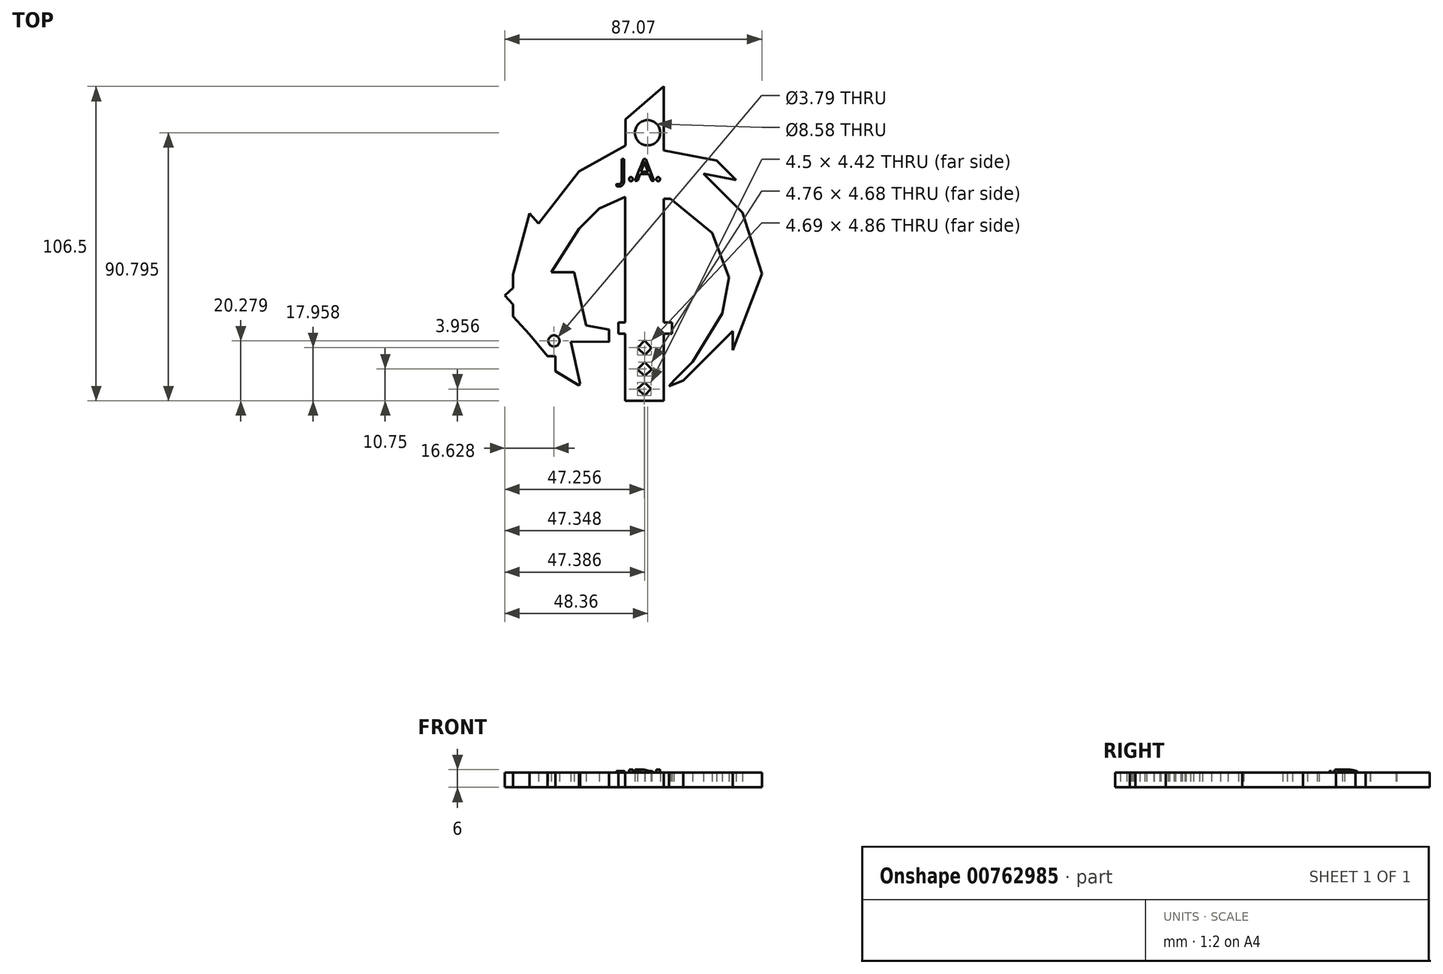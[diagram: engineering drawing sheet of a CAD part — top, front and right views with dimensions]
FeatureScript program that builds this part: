
annotation { "Feature Type Name" : "Feature", "Feature Type Description" : "" }
export const myFeature = defineFeature(function(context is Context, id is Id, definition is map)
    precondition{}
    {
        {
            var Q0;
            Q0=qCreatedBy(makeId("Top.planeOp"),FACE);
            var sketch = newSketch(context, id + "F0", { "sketchPlane" : qUnion([Q0])});
            skLineSegment(sketch, "E0", {"start": v(-26.03, -12.55) * mm, "end": v(-22.86, -26.95) * mm});
            skLineSegment(sketch, "E1", {"start": v(-22.86, -26.95) * mm, "end": v(-23.17, -27.48) * mm});
            skLineSegment(sketch, "E2", {"start": v(-23.17, -27.48) * mm, "end": v(-31.28, -22.62) * mm});
            skLineSegment(sketch, "E3", {"start": v(-31.28, -17.57) * mm, "end": v(-33.96, -17.57) * mm});
            skLineSegment(sketch, "E4", {"start": v(-33.96, -17.57) * mm, "end": v(-40.04, -10.17) * mm});
            skLineSegment(sketch, "E5", {"start": v(-40.04, -10.17) * mm, "end": v(-45.59, -4.1) * mm});
            skLineSegment(sketch, "E6", {"start": v(-45.59, -4.1) * mm, "end": v(-45.59, 0) * mm});
            skLineSegment(sketch, "E7", {"start": v(-45.59, 0) * mm, "end": v(-40.04, -6.08) * mm});
            skLineSegment(sketch, "E8", {"start": v(-40.04, -6.08) * mm, "end": v(-45.59, 0) * mm});
            skLineSegment(sketch, "E9", {"start": v(-45.59, 0) * mm, "end": v(-48.36, 3.04) * mm});
            skLineSegment(sketch, "E10", {"start": v(-48.36, 3.04) * mm, "end": v(-45.59, 5.57) * mm});
            skLineSegment(sketch, "E11", {"start": v(-45.59, 5.57) * mm, "end": v(-45.59, 10.17) * mm});
            skLineSegment(sketch, "E12", {"start": v(-45.59, 10.17) * mm, "end": v(-40.04, 30.79) * mm});
            skLineSegment(sketch, "E13", {"start": v(-40.04, 30.79) * mm, "end": v(-37, 27.45) * mm});
            skLineSegment(sketch, "E14", {"start": v(-37, 27.45) * mm, "end": v(-23.17, 45.06) * mm});
            skLineSegment(sketch, "E15", {"start": v(-23.17, 45.06) * mm, "end": v(-7.53, 53.78) * mm});
            skLineSegment(sketch, "E16", {"start": v(5.42, -9.9) * mm, "end": v(8.32, -9.9) * mm});
            skLineSegment(sketch, "E17", {"start": v(8.32, -9.9) * mm, "end": v(8.32, -6.08) * mm});
            skLineSegment(sketch, "E18", {"start": v(-7.53, 62.76) * mm, "end": v(5.42, 73.86) * mm});
            skLineSegment(sketch, "E19", {"start": v(5.42, 73.86) * mm, "end": v(5.42, -3.04) * mm});
            skLineSegment(sketch, "E20", {"start": v(5.42, -3.04) * mm, "end": v(0, 0) * mm});
            skLineSegment(sketch, "E21", {"start": v(5.42, -9.9) * mm, "end": v(5.42, -32.64) * mm});
            skLineSegment(sketch, "E22", {"start": v(-9.9, -6.08) * mm, "end": v(8.32, -6.08) * mm});
            skLineSegment(sketch, "E23", {"start": v(7.8, 35.8) * mm, "end": v(21.8, 24.18) * mm});
            skLineSegment(sketch, "E24", {"start": v(21.8, 24.18) * mm, "end": v(27.62, 9.12) * mm});
            skLineSegment(sketch, "E25", {"start": v(27.62, 9.12) * mm, "end": v(25.24, -3.04) * mm});
            skLineSegment(sketch, "E26", {"start": v(25.24, -3.04) * mm, "end": v(15.2, -19.42) * mm});
            skLineSegment(sketch, "E27", {"start": v(15.2, -19.42) * mm, "end": v(8.85, -25.77) * mm});
            skLineSegment(sketch, "E28", {"start": v(12.02, -25.77) * mm, "end": v(28.8, -8.98) * mm});
            skPoint(sketch, "E28.startSnap0", {"position": v(12.02, -22.6) * mm});
            skLineSegment(sketch, "E29", {"start": v(28.8, -8.98) * mm, "end": v(28.8, -15.46) * mm});
            skLineSegment(sketch, "E30", {"start": v(28.8, -15.46) * mm, "end": v(38.71, 10.44) * mm});
            skLineSegment(sketch, "E31", {"start": v(38.71, 10.44) * mm, "end": v(32.1, 31.05) * mm});
            skLineSegment(sketch, "E32", {"start": v(32.1, 31.05) * mm, "end": v(18.9, 44.26) * mm});
            skLineSegment(sketch, "E33", {"start": v(18.9, 44.26) * mm, "end": v(30, 42.15) * mm});
            skLineSegment(sketch, "E34", {"start": v(30, 42.15) * mm, "end": v(23.39, 48.76) * mm});
            skLineSegment(sketch, "E35", {"start": v(23.39, 48.76) * mm, "end": v(8.85, 51.52) * mm});
            skLineSegment(sketch, "E36", {"start": v(8.85, 51.52) * mm, "end": v(5.42, 52.18) * mm});
            skLineSegment(sketch, "E37", {"start": v(8.85, -25.77) * mm, "end": v(7.2, -27.75) * mm});
            skLineSegment(sketch, "E38", {"start": v(7.2, -27.75) * mm, "end": v(12.02, -25.77) * mm});
            skLineSegment(sketch, "E39", {"start": v(-26.03, -12.55) * mm, "end": v(-22.86, -12.59) * mm});
            skLineSegment(sketch, "E40", {"start": v(-22.86, -12.59) * mm, "end": v(-13.06, -12.7) * mm});
            skLineSegment(sketch, "E41", {"start": v(-13.06, -12.7) * mm, "end": v(-13.06, -8.59) * mm});
            skLineSegment(sketch, "E42", {"start": v(-13.06, -8.59) * mm, "end": v(-16.32, -7.97) * mm});
            skLineSegment(sketch, "E43", {"start": v(-16.32, -7.97) * mm, "end": v(-20.86, -7.1) * mm});
            skLineSegment(sketch, "E44", {"start": v(-20.86, -7.1) * mm, "end": v(-23.17, 3.39) * mm});
            skLineSegment(sketch, "E45", {"start": v(-23.17, 3.39) * mm, "end": v(-24.83, 10.91) * mm});
            skLineSegment(sketch, "E46", {"start": v(-24.83, 10.91) * mm, "end": v(-32.64, 10.91) * mm});
            skLineSegment(sketch, "E47", {"start": v(-32.64, 10.91) * mm, "end": v(-23.17, 25.64) * mm});
            skLineSegment(sketch, "E48", {"start": v(-23.17, 25.64) * mm, "end": v(-16.32, 32.49) * mm});
            skLineSegment(sketch, "E49", {"start": v(-16.32, 32.49) * mm, "end": v(-7.53, 36.43) * mm});
            skLineSegment(sketch, "E50", {"start": v(-31.28, -17.57) * mm, "end": v(-31.28, -22.62) * mm});
            skLineSegment(sketch, "E51", {"start": v(7.8, 35.8) * mm, "end": v(5.42, 35.83) * mm});
            skPoint(sketch, "E51.endSnap0", {"position": v(5.42, 35.41) * mm});
            skLineSegment(sketch, "E52", {"start": v(-7.6, -6.08) * mm, "end": v(5.42, -6.08) * mm});
            skLineSegment(sketch, "E53", {"start": v(5.42, -6.08) * mm, "end": v(5.42, -3.04) * mm});
            skLineSegment(sketch, "E54", {"start": v(0, 0) * mm, "end": v(-7.6, -3.04) * mm});
            skLineSegment(sketch, "E55", {"start": v(-7.6, -3.04) * mm, "end": v(-7.53, 62.76) * mm});
            skLineSegment(sketch, "E56", {"start": v(-7.6, -3.04) * mm, "end": v(-7.6, -6.08) * mm});
            skLineSegment(sketch, "E57", {"start": v(-9.9, -6.08) * mm, "end": v(-9.9, -9.9) * mm});
            skLineSegment(sketch, "E58", {"start": v(-9.9, -9.9) * mm, "end": v(-7.55, -9.9) * mm});
            skLineSegment(sketch, "E59", {"start": v(-7.55, -9.9) * mm, "end": v(-7.55, -32.64) * mm});
            skLineSegment(sketch, "E60", {"start": v(5.42, -32.64) * mm, "end": v(-7.55, -32.64) * mm});
            skCircle(sketch, "E61", {"center": v(-31.73, -12.36) * mm, "radius": 1.9 * mm});
            skLineSegment(sketch, "E62", {"start": v(-1.02, -12.25) * mm, "end": v(-3.35, -14.78) * mm});
            skLineSegment(sketch, "E63", {"start": v(-3.35, -14.78) * mm, "end": v(-0.83, -17.11) * mm});
            skLineSegment(sketch, "E64", {"start": v(-0.83, -17.11) * mm, "end": v(1.33, -14.78) * mm});
            skLineSegment(sketch, "E65", {"start": v(1.33, -14.78) * mm, "end": v(-1.02, -12.25) * mm});
            skLineSegment(sketch, "E66", {"start": v(-1.02, -19.55) * mm, "end": v(-3.35, -21.98) * mm});
            skLineSegment(sketch, "E67", {"start": v(-3.35, -21.98) * mm, "end": v(-1.02, -24.23) * mm});
            skLineSegment(sketch, "E68", {"start": v(-1.02, -24.23) * mm, "end": v(1.4, -21.98) * mm});
            skLineSegment(sketch, "E69", {"start": v(1.4, -21.98) * mm, "end": v(-1.02, -19.55) * mm});
            skLineSegment(sketch, "E70", {"start": v(-1.02, -26.47) * mm, "end": v(-3.35, -28.65) * mm});
            skLineSegment(sketch, "E71", {"start": v(-3.35, -28.65) * mm, "end": v(-1.02, -30.9) * mm});
            skLineSegment(sketch, "E72", {"start": v(-1.02, -30.9) * mm, "end": v(1.15, -28.65) * mm});
            skLineSegment(sketch, "E73", {"start": v(1.15, -28.65) * mm, "end": v(-1.02, -26.47) * mm});
            skCircle(sketch, "E74", {"center": v(0, 58.16) * mm, "radius": 4.29 * mm});
            skSolve(sketch);
        }
        {
            var Q0;
            {var subQ6=sQuery(id+"F0.wireOp",EDGE,"E18");var subQ8=sQuery(id+"F0.wireOp",EDGE,"E20");var subQ9=makeQuery(id+"F0.imprint","IMPRINT",EDGE,{"derivedFrom":subQ8});Q0=qUnion([makeQuery(id+"F0.imprint","IMPRINT",FACE,{"disambiguationData":[TD([[makeQuery(id+"F0.imprint","IMPRINT",EDGE,{"derivedFrom":sQuery(id+"F0.wireOp",EDGE,"E23")}),1.0]])]}),makeQuery(id+"F0.imprint","IMPRINT",FACE,{"disambiguationData":[TD([[makeQuery(id+"F0.imprint","IMPRINT",EDGE,{"derivedFrom":sQuery(id+"F0.wireOp",EDGE,"E0")}),-1.0]])]}),makeQuery(id+"F0.imprint","IMPRINT",FACE,{"disambiguationData":[TD([[subQ9,1.0]])]}),makeQuery(id+"F0.imprint","IMPRINT",FACE,{"disambiguationData":[TD([[makeQuery(id+"F0.imprint","IMPRINT",EDGE,{"derivedFrom":sQuery(id+"F0.wireOp",EDGE,"E16")}),1.0]])]}),makeQuery(id+"F0.imprint","IMPRINT",FACE,{"disambiguationData":[TD([[makeQuery(id+"F0.imprint","IMPRINT",EDGE,{"derivedFrom":subQ6}),-1.0]])]})]);}
            extrude(context, id + "F1", {"entities" : qUnion([Q0]), "depth" : 5 * mm, "offsetDistance" : 25 * mm});
        }
        {
            var Q0;
            Q0=makeQuery(id+"F1.opExtrude","CAP_FACE",FACE,{"disambiguationData":[OSD([sQuery(id+"F0.wireOp",EDGE,"E0"),sQuery(id+"F0.wireOp",EDGE,"E1"),sQuery(id+"F0.wireOp",EDGE,"E2"),sQuery(id+"F0.wireOp",EDGE,"E3"),sQuery(id+"F0.wireOp",EDGE,"E4"),sQuery(id+"F0.wireOp",EDGE,"E5"),sQuery(id+"F0.wireOp",EDGE,"E6"),sQuery(id+"F0.wireOp",EDGE,"E9"),sQuery(id+"F0.wireOp",EDGE,"E10"),sQuery(id+"F0.wireOp",EDGE,"E11"),sQuery(id+"F0.wireOp",EDGE,"E12"),sQuery(id+"F0.wireOp",EDGE,"E13"),sQuery(id+"F0.wireOp",EDGE,"E14"),sQuery(id+"F0.wireOp",EDGE,"E15"),sQuery(id+"F0.wireOp",EDGE,"E16"),sQuery(id+"F0.wireOp",EDGE,"E17"),sQuery(id+"F0.wireOp",EDGE,"E18"),sQuery(id+"F0.wireOp",EDGE,"E19"),sQuery(id+"F0.wireOp",EDGE,"E21"),sQuery(id+"F0.wireOp",EDGE,"E22"),sQuery(id+"F0.wireOp",EDGE,"E23"),sQuery(id+"F0.wireOp",EDGE,"E24"),sQuery(id+"F0.wireOp",EDGE,"E25"),sQuery(id+"F0.wireOp",EDGE,"E26"),sQuery(id+"F0.wireOp",EDGE,"E27"),sQuery(id+"F0.wireOp",EDGE,"E28"),sQuery(id+"F0.wireOp",EDGE,"E29"),sQuery(id+"F0.wireOp",EDGE,"E30"),sQuery(id+"F0.wireOp",EDGE,"E31"),sQuery(id+"F0.wireOp",EDGE,"E32"),sQuery(id+"F0.wireOp",EDGE,"E33"),sQuery(id+"F0.wireOp",EDGE,"E34"),sQuery(id+"F0.wireOp",EDGE,"E35"),sQuery(id+"F0.wireOp",EDGE,"E36"),sQuery(id+"F0.wireOp",EDGE,"E37"),sQuery(id+"F0.wireOp",EDGE,"E38"),sQuery(id+"F0.wireOp",EDGE,"E39"),sQuery(id+"F0.wireOp",EDGE,"E40"),sQuery(id+"F0.wireOp",EDGE,"E41"),sQuery(id+"F0.wireOp",EDGE,"E42"),sQuery(id+"F0.wireOp",EDGE,"E43"),sQuery(id+"F0.wireOp",EDGE,"E44"),sQuery(id+"F0.wireOp",EDGE,"E45"),sQuery(id+"F0.wireOp",EDGE,"E46"),sQuery(id+"F0.wireOp",EDGE,"E47"),sQuery(id+"F0.wireOp",EDGE,"E48"),sQuery(id+"F0.wireOp",EDGE,"E49"),sQuery(id+"F0.wireOp",EDGE,"E50"),sQuery(id+"F0.wireOp",EDGE,"E51"),sQuery(id+"F0.wireOp",EDGE,"E53"),sQuery(id+"F0.wireOp",EDGE,"E55"),sQuery(id+"F0.wireOp",EDGE,"E56"),sQuery(id+"F0.wireOp",EDGE,"E57"),sQuery(id+"F0.wireOp",EDGE,"E58"),sQuery(id+"F0.wireOp",EDGE,"E59"),sQuery(id+"F0.wireOp",EDGE,"E60"),sQuery(id+"F0.wireOp",EDGE,"E61"),sQuery(id+"F0.wireOp",EDGE,"E62"),sQuery(id+"F0.wireOp",EDGE,"E63"),sQuery(id+"F0.wireOp",EDGE,"E64"),sQuery(id+"F0.wireOp",EDGE,"E65"),sQuery(id+"F0.wireOp",EDGE,"E66"),sQuery(id+"F0.wireOp",EDGE,"E67"),sQuery(id+"F0.wireOp",EDGE,"E68"),sQuery(id+"F0.wireOp",EDGE,"E69"),sQuery(id+"F0.wireOp",EDGE,"E70"),sQuery(id+"F0.wireOp",EDGE,"E71"),sQuery(id+"F0.wireOp",EDGE,"E72"),sQuery(id+"F0.wireOp",EDGE,"E73"),sQuery(id+"F0.wireOp",EDGE,"E74")])],"isStart":false});
            var sketch = newSketch(context, id + "F2", { "sketchPlane" : qUnion([Q0])});
            skText(sketch, "E75", { "text": "J.A.", "fontName": "OpenSans-Regular.ttf"});
            const initialGuessF2  = {"E75": [-0.00976, 0.0419, 1, 0, 0.0074]};
            skSetInitialGuess(sketch, initialGuessF2);
            skSolve(sketch);
        }
        {
            var Q0;
            Q0 = qSketchRegion(id + "F2", true);
            extrude(context, id + "F3", {"entities" : qUnion([Q0]), "operationType" : NewBodyOperationType.ADD, "depth" : 1 * mm, "offsetDistance" : 25 * mm});
        }
        {
            var Q0;
            Q0=makeQuery(id+"F3.opExtrude","CAP_EDGE",EDGE,{"disambiguationData":[OSD([sQuery(id+"F2.wireOp",EDGE,"E75.sketch_text.stroke-24")])],"isStart":false});
            var Q1;
            Q1=makeQuery(id+"F3.opExtrude","CAP_EDGE",EDGE,{"disambiguationData":[OSD([sQuery(id+"F2.wireOp",EDGE,"E75.sketch_text.stroke-5")])],"isStart":false});
            fillet(context, id + "F4", {"entities" : qUnion([Q0, Q1]), "radius" : 5 * mm, "tangentPropagation" : true, "allowEdgeOverflow" : false});
        }
    });
